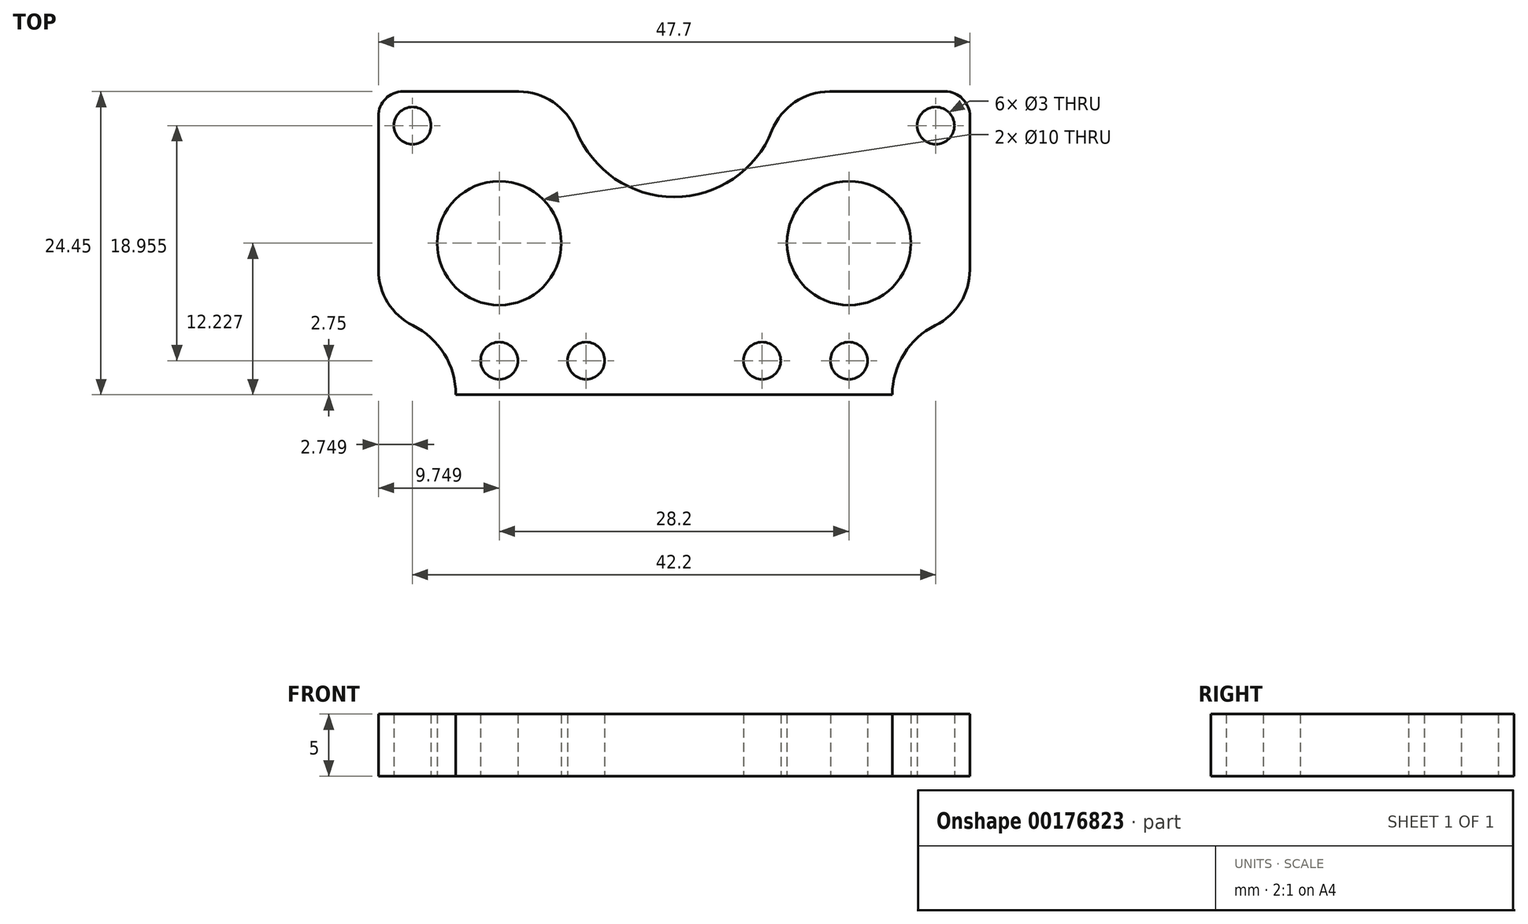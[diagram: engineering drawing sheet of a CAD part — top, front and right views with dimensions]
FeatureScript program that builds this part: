
annotation { "Feature Type Name" : "Feature", "Feature Type Description" : "" }
export const myFeature = defineFeature(function(context is Context, id is Id, definition is map)
    precondition{}
    {
        {
            var Q0;
            Q0=qCreatedBy(makeId("Top.planeOp"),FACE);
            var sketch = newSketch(context, id + "F0", { "sketchPlane" : qUnion([Q0])});
            skCircle(sketch, "E0", {"center": v(-28.56, 18.95) * mm, "radius": 1.5 * mm});
            skCircle(sketch, "E1", {"center": v(13.64, 18.95) * mm, "radius": 1.5 * mm});
            skLineSegment(sketch, "E2", {"start": v(-28.56, 18.95) * mm, "end": v(-28.56, 0) * mm, "construction": true});
            skCircle(sketch, "E3", {"center": v(-21.56, 0) * mm, "radius": 1.5 * mm});
            skCircle(sketch, "E4", {"center": v(6.64, 0) * mm, "radius": 1.5 * mm});
            skCircle(sketch, "E5", {"center": v(-14.56, 0) * mm, "radius": 1.5 * mm});
            skCircle(sketch, "E6", {"center": v(-0.36, 0) * mm, "radius": 1.5 * mm});
            skLineSegment(sketch, "E7.bottom", {"start": v(14.39, 21.7) * mm, "end": v(5.08, 21.7) * mm});
            skLineSegment(sketch, "E7.top", {"start": v(10.14, -2.75) * mm, "end": v(-25.06, -2.75) * mm});
            skLineSegment(sketch, "E7.left", {"start": v(16.39, 19.7) * mm, "end": v(16.39, 7.33) * mm});
            skLineSegment(sketch, "E7.right", {"start": v(-31.31, 19.7) * mm, "end": v(-31.31, 7.33) * mm});
            skPoint(sketch, "E7.middle", {"position": v(-7.46, 9.48) * mm});
            skArc(sketch, "E8", {"start": v(-15.36, 18.56) * mm, "mid": v(-7.46, 13.2) * mm, "end": v(0.43, 18.56) * mm});
            skLineSegment(sketch, "E9.trimOffspring", {"start": v(-20, 21.7) * mm, "end": v(-29.31, 21.7) * mm});
            skLineSegment(sketch, "E10", {"start": v(-28.56, 0) * mm, "end": v(-21.56, 0) * mm, "construction": true});
            skLineSegment(sketch, "E11", {"start": v(-25.06, 0) * mm, "end": v(-25.06, -2.75) * mm, "construction": true});
            skLineSegment(sketch, "E12", {"start": v(-25.06, -2.75) * mm, "end": v(-25.06, -1.37) * mm});
            skArc(sketch, "E13", {"start": v(-25.06, -2.75) * mm, "mid": v(-26, 0.54) * mm, "end": v(-28.53, 2.85) * mm});
            skArc(sketch, "E14", {"start": v(13.61, 2.85) * mm, "mid": v(11.08, 0.54) * mm, "end": v(10.14, -2.75) * mm});
            skPoint(sketch, "E15.visualSharp", {"position": v(-15.96, 21.7) * mm});
            skArc(sketch, "E15.filletArc", {"start": v(-15.36, 18.56) * mm, "mid": v(-17.2, 20.84) * mm, "end": v(-20, 21.7) * mm});
            skPoint(sketch, "E16.visualSharp", {"position": v(1.04, 21.7) * mm});
            skArc(sketch, "E16.filletArc", {"start": v(5.08, 21.7) * mm, "mid": v(2.27, 20.84) * mm, "end": v(0.43, 18.56) * mm});
            skArc(sketch, "E17.filletArc", {"start": v(-31.31, 7.33) * mm, "mid": v(-30.56, 4.7) * mm, "end": v(-28.53, 2.85) * mm});
            skArc(sketch, "E18.filletArc", {"start": v(13.61, 2.85) * mm, "mid": v(15.64, 4.7) * mm, "end": v(16.39, 7.33) * mm});
            skPoint(sketch, "E19.visualSharp", {"position": v(-31.31, 21.7) * mm});
            skArc(sketch, "E19.filletArc", {"start": v(-29.31, 21.7) * mm, "mid": v(-30.73, 21.12) * mm, "end": v(-31.31, 19.7) * mm});
            skPoint(sketch, "E20.visualSharp", {"position": v(16.39, 21.7) * mm});
            skArc(sketch, "E20.filletArc", {"start": v(16.39, 19.7) * mm, "mid": v(15.8, 21.12) * mm, "end": v(14.39, 21.7) * mm});
            skLineSegment(sketch, "E21", {"start": v(-28.56, 18.95) * mm, "end": v(-14.56, 0) * mm, "construction": true});
            skLineSegment(sketch, "E22", {"start": v(-0.36, 0) * mm, "end": v(13.64, 18.95) * mm, "construction": true});
            skCircle(sketch, "E23", {"center": v(-21.56, 9.48) * mm, "radius": 5 * mm});
            skCircle(sketch, "E24", {"center": v(6.64, 9.48) * mm, "radius": 5 * mm});
            skSolve(sketch);
        }
        {
            var Q0;
            Q0=makeQuery(id+"F0.imprint","IMPRINT",FACE,{"disambiguationData":[TD([[makeQuery(id+"F0.imprint","IMPRINT",EDGE,{"derivedFrom":sQuery(id+"F0.wireOp",EDGE,"E0")}),-1.0]])]});
            extrude(context, id + "F1", {"entities" : qUnion([Q0]), "depth" : 5 * mm});
        }
    });
